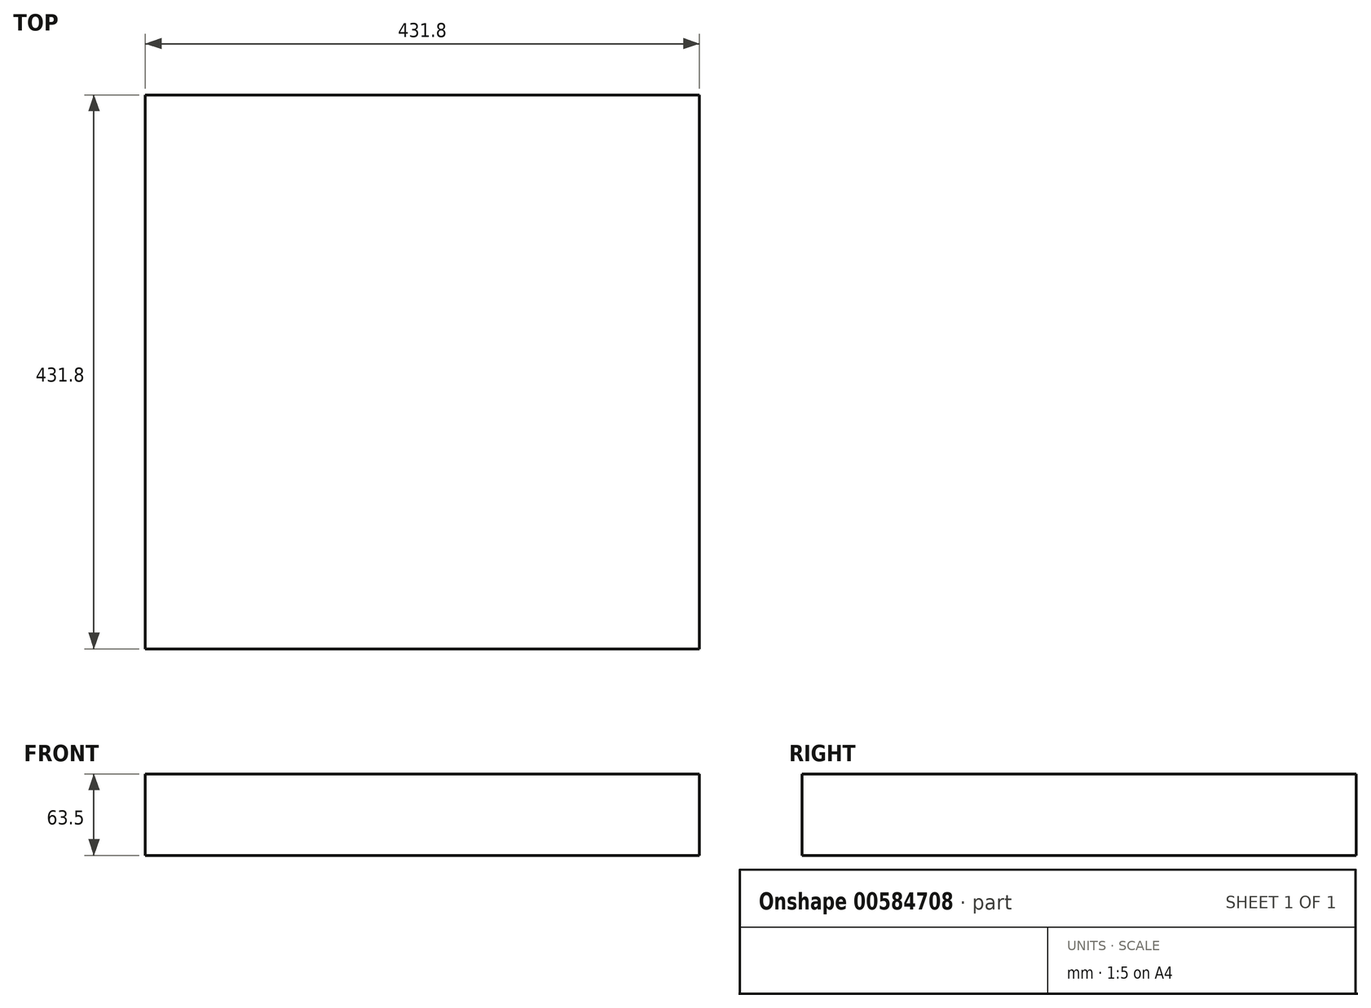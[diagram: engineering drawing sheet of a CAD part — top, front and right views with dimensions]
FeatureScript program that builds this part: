
annotation { "Feature Type Name" : "Feature", "Feature Type Description" : "" }
export const myFeature = defineFeature(function(context is Context, id is Id, definition is map)
    precondition{}
    {
        {
            var Q0;
            Q0=qCreatedBy(makeId("Top.planeOp"),FACE);
            var sketch = newSketch(context, id + "F0", { "sketchPlane" : qUnion([Q0])});
            skLineSegment(sketch, "E0.bottom", {"start": v(215.9, -215.9) * mm, "end": v(-215.9, -215.9) * mm});
            skLineSegment(sketch, "E0.top", {"start": v(215.9, 215.9) * mm, "end": v(-215.9, 215.9) * mm});
            skLineSegment(sketch, "E0.left", {"start": v(215.9, -215.9) * mm, "end": v(215.9, 215.9) * mm});
            skLineSegment(sketch, "E0.right", {"start": v(-215.9, -215.9) * mm, "end": v(-215.9, 215.9) * mm});
            skPoint(sketch, "E0.middle", {"position": v(0, 0) * mm});
            skSolve(sketch);
        }
        {
            var Q0;
            Q0 = qSketchRegion(id + "F0", true);
            extrude(context, id + "F1", {"entities" : qUnion([Q0]), "depth" : 63.5 * mm, "offsetDistance" : 25.4 * mm});
        }
    });
